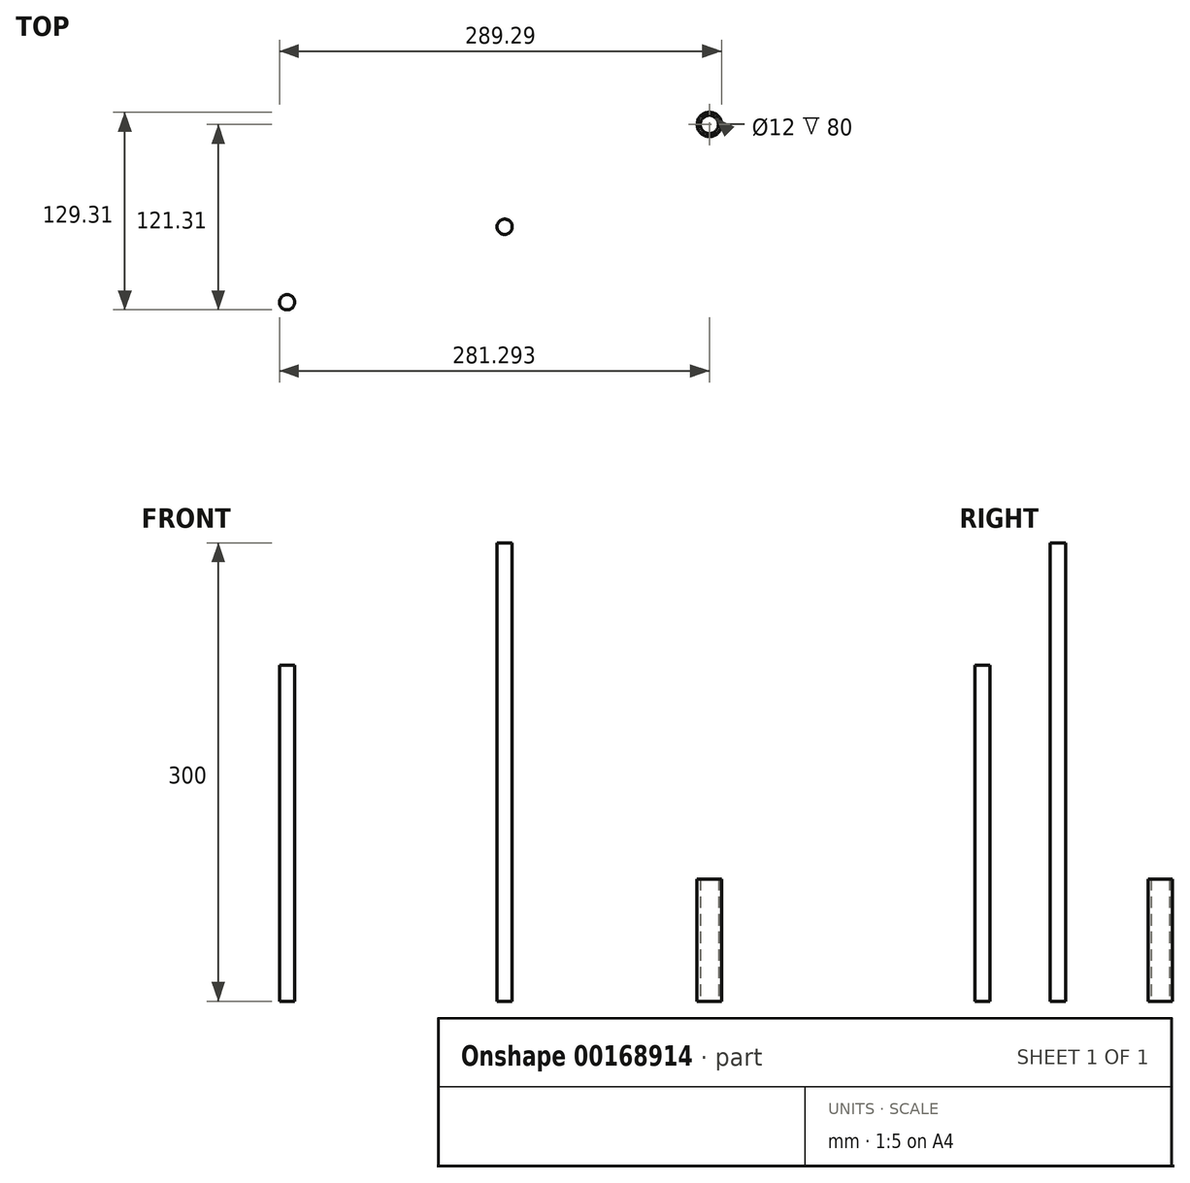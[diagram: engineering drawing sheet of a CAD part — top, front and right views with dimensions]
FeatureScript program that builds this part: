
annotation { "Feature Type Name" : "Feature", "Feature Type Description" : "" }
export const myFeature = defineFeature(function(context is Context, id is Id, definition is map)
    precondition{}
    {
        {
            var Q0;
            Q0=qCreatedBy(makeId("Top.planeOp"),FACE);
            var sketch = newSketch(context, id + "F0", { "sketchPlane" : qUnion([Q0])});
            skCircle(sketch, "E0", {"center": v(0, 0) * mm, "radius": 5 * mm});
            skSolve(sketch);
        }
        {
            var Q0;
            Q0=makeQuery(id+"F0.imprint","IMPRINT",FACE,{"disambiguationData":[TD([[makeQuery(id+"F0.imprint","IMPRINT",EDGE,{"derivedFrom":sQuery(id+"F0.wireOp",EDGE,"E0")}),1.0]])]});
            extrude(context, id + "F1", {"entities" : qUnion([Q0]), "depth" : 300 * mm});
        }
        {
            var Q0;
            Q0=qCreatedBy(makeId("Top.planeOp"),FACE);
            var sketch = newSketch(context, id + "F2", { "sketchPlane" : qUnion([Q0])});
            skCircle(sketch, "E1", {"center": v(-142.33, -49.37) * mm, "radius": 5 * mm});
            skSolve(sketch);
        }
        {
            var Q0;
            Q0=makeQuery(id+"F2.imprint","IMPRINT",FACE,{"disambiguationData":[TD([[makeQuery(id+"F2.imprint","IMPRINT",EDGE,{"derivedFrom":sQuery(id+"F2.wireOp",EDGE,"E1")}),1.0]])]});
            extrude(context, id + "F3", {"entities" : qUnion([Q0]), "depth" : 220 * mm});
        }
        {
            var Q0;
            Q0=qCreatedBy(makeId("Top.planeOp"),FACE);
            var sketch = newSketch(context, id + "F4", { "sketchPlane" : qUnion([Q0])});
            skCircle(sketch, "E2", {"center": v(133.96, 66.94) * mm, "radius": 6 * mm});
            skCircle(sketch, "E3", {"center": v(133.96, 66.94) * mm, "radius": 8 * mm});
            skSolve(sketch);
        }
        {
            var Q0;
            Q0=makeQuery(id+"F4.imprint","IMPRINT",FACE,{"disambiguationData":[TD([[makeQuery(id+"F4.imprint","IMPRINT",EDGE,{"derivedFrom":sQuery(id+"F4.wireOp",EDGE,"E2")}),-1.0]])]});
            extrude(context, id + "F5", {"entities" : qUnion([Q0]), "depth" : 80 * mm});
        }
    });
